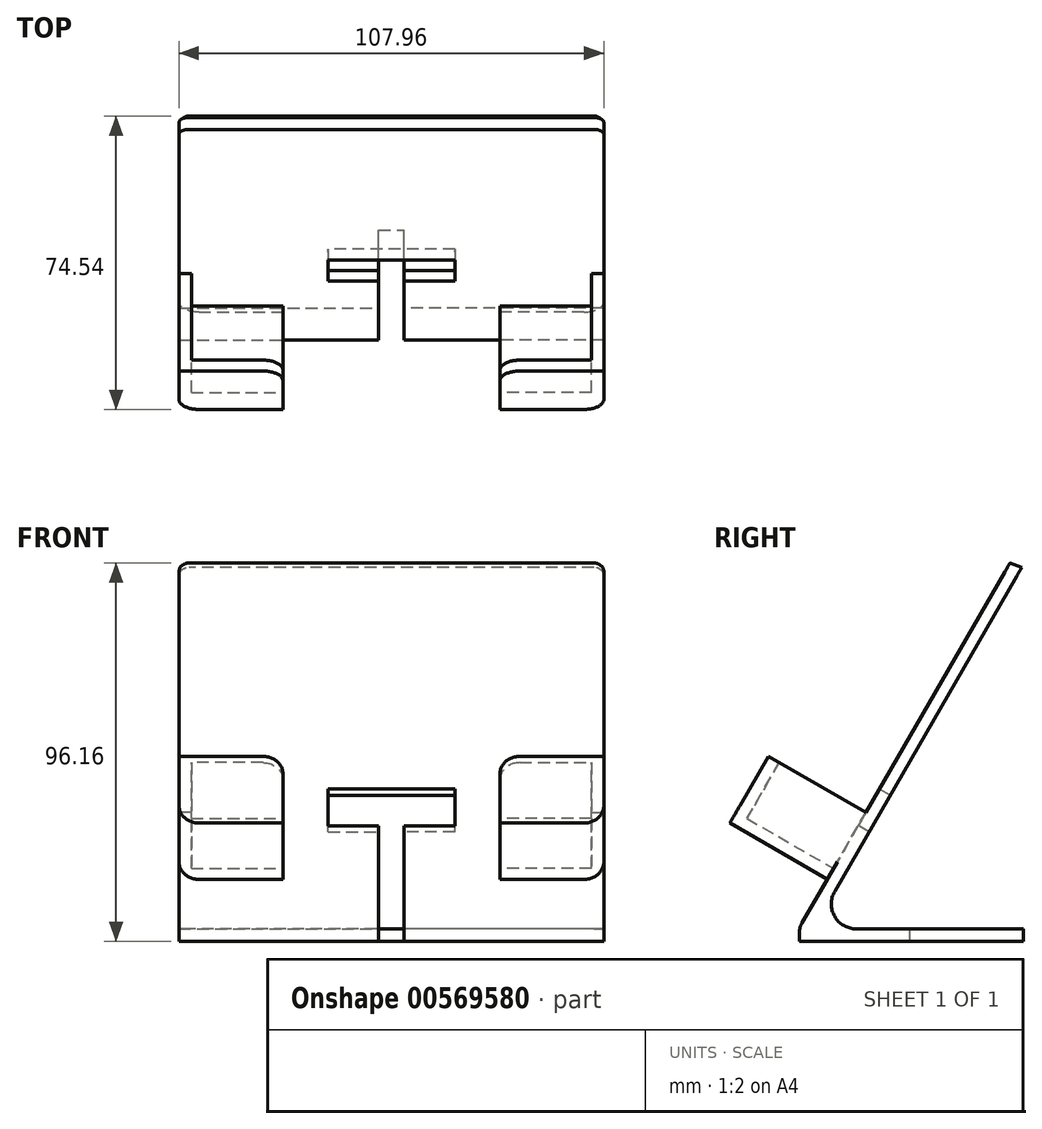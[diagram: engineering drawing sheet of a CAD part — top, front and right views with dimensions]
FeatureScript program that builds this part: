
annotation { "Feature Type Name" : "Feature", "Feature Type Description" : "" }
export const myFeature = defineFeature(function(context is Context, id is Id, definition is map)
    precondition{}
    {
        {
            var Q0;
            Q0=qCreatedBy(makeId("Right.planeOp"),FACE);
            var sketch = newSketch(context, id + "F0", { "sketchPlane" : qUnion([Q0])});
            skLineSegment(sketch, "E0", {"start": v(56.9, 0) * mm, "end": v(0, 0) * mm});
            skLineSegment(sketch, "E1", {"start": v(0, 0) * mm, "end": v(0, 3.5) * mm});
            skPoint(sketch, "E2.visualSharp", {"position": v(0, 0) * mm});
            skLineSegment(sketch, "E3", {"start": v(0, 3.5) * mm, "end": v(53.5, 96.16) * mm});
            skLineSegment(sketch, "E4.0", {"start": v(8.98, 12.7) * mm, "end": v(56.54, 95.07) * mm});
            skLineSegment(sketch, "E4.2", {"start": v(56.9, 3.18) * mm, "end": v(14.48, 3.17) * mm});
            skLineSegment(sketch, "E5", {"start": v(53.5, 96.16) * mm, "end": v(56.54, 95.07) * mm});
            skLineSegment(sketch, "E6", {"start": v(56.9, 3.18) * mm, "end": v(56.9, 0) * mm});
            skPoint(sketch, "E7.visualSharp", {"position": v(3.48, 3.17) * mm});
            skArc(sketch, "E7.filletArc", {"start": v(8.98, 12.7) * mm, "mid": v(8.98, 6.35) * mm, "end": v(14.48, 3.17) * mm});
            skSolve(sketch);
        }
        {
            var Q0;
            Q0=qSketchRegion(id+"F0",true);
            extrude(context, id + "F1", {"entities" : qUnion([Q0]), "depth" : 53.97 * mm, "offsetDistance" : 25.4 * mm});
        }
        {
            var Q0;
            {var subQ0=makeQuery(id+"F1.opExtrude","SWEPT_FACE",FACE,{"disambiguationData":[OSD([sQuery(id+"F0.wireOp",EDGE,"E3")])]});Q0=makeQuery(id+"F12.boolean.opBoolean","MERGE",FACE,{"derivedFrom":[subQ0,makeQuery(id+"F12.opPattern","COPY",FACE,{"derivedFrom":subQ0,"instanceName":"1"})]});}
            var sketch = newSketch(context, id + "F2", { "sketchPlane" : qUnion([Q0])});
            skLineSegment(sketch, "E8", {"start": v(53.98, 17.22) * mm, "end": v(27.55, 17.22) * mm});
            skLineSegment(sketch, "E9", {"start": v(53.98, 17.22) * mm, "end": v(53.98, 36.77) * mm});
            skLineSegment(sketch, "E10.0", {"start": v(50.8, 20.4) * mm, "end": v(50.8, 36.77) * mm});
            skLineSegment(sketch, "E10.1", {"start": v(50.8, 20.4) * mm, "end": v(27.55, 20.4) * mm});
            skLineSegment(sketch, "E11", {"start": v(50.8, 36.77) * mm, "end": v(53.98, 36.77) * mm});
            skLineSegment(sketch, "E12", {"start": v(27.55, 20.4) * mm, "end": v(27.55, 17.22) * mm});
            skSolve(sketch);
        }
        {
            var Q0;
            Q0=qSketchRegion(id+"F2",true);
            extrude(context, id + "F3", {"entities" : qUnion([Q0]), "operationType" : NewBodyOperationType.ADD, "depth" : 25.4 * mm, "offsetDistance" : 25.4 * mm});
        }
        {
            var Q0;
            {var subQ0=makeQuery(id+"F1.opExtrude","SWEPT_FACE",FACE,{"disambiguationData":[OSD([sQuery(id+"F0.wireOp",EDGE,"E3")])]});Q0=makeQuery(id+"F12.boolean.opBoolean","MERGE",FACE,{"derivedFrom":[subQ0,makeQuery(id+"F12.opPattern","COPY",FACE,{"derivedFrom":subQ0,"instanceName":"1"})]});}
            var sketch = newSketch(context, id + "F4", { "sketchPlane" : qUnion([Q0])});
            skLineSegment(sketch, "E13.bottom", {"start": v(0, 43.7) * mm, "end": v(16.1, 43.7) * mm});
            skLineSegment(sketch, "E13.top", {"start": v(0, 32.91) * mm, "end": v(16.1, 32.91) * mm});
            skLineSegment(sketch, "E13.left", {"start": v(0, 43.7) * mm, "end": v(0, 32.91) * mm});
            skLineSegment(sketch, "E13.right", {"start": v(16.1, 43.7) * mm, "end": v(16.1, 32.91) * mm});
            skSolve(sketch);
        }
        {
            var Q0;
            Q0=qSketchRegion(id+"F4",true);
            extrude(context, id + "F5", {"entities" : qUnion([Q0]), "operationType" : NewBodyOperationType.REMOVE, "endBound" : BoundingType.UP_TO_NEXT, "oppositeDirection" : true, "depth" : 25.4 * mm});
        }
        {
            var Q0;
            Q0=qCreatedBy(makeId("Top.planeOp"),FACE);
            var sketch = newSketch(context, id + "F6", { "sketchPlane" : qUnion([Q0])});
            skLineSegment(sketch, "E14.bottom", {"start": v(0, 0) * mm, "end": v(3.24, 0) * mm});
            skLineSegment(sketch, "E14.top", {"start": v(0, 27.97) * mm, "end": v(3.24, 27.97) * mm});
            skLineSegment(sketch, "E14.left", {"start": v(0, 0) * mm, "end": v(0, 27.97) * mm});
            skLineSegment(sketch, "E14.right", {"start": v(3.24, 0) * mm, "end": v(3.24, 27.97) * mm});
            skSolve(sketch);
        }
        {
            var Q0;
            Q0=qSketchRegion(id+"F6",true);
            var Q1;
            {var subQ0=makeQuery(id+"F5.boolean.opBoolean","COPY",FACE,{"derivedFrom":makeQuery(id+"F5.opExtrude","SWEPT_FACE",FACE,{"disambiguationData":[OSD([sQuery(id+"F4.wireOp",EDGE,"E13.top")])]})});Q1=makeQuery(id+"F12.boolean.opBoolean","MERGE",FACE,{"derivedFrom":[subQ0,makeQuery(id+"F12.opPattern","COPY",FACE,{"derivedFrom":subQ0,"instanceName":"1"})]});}
            extrude(context, id + "F7", {"entities" : qUnion([Q0]), "operationType" : NewBodyOperationType.REMOVE, "endBound" : BoundingType.UP_TO_SURFACE, "endBoundEntityFace" : qUnion([Q1]), "depth" : 25.4 * mm, "offsetDistance" : 25.4 * mm});
        }
        {
            var Q0;
            Q0=makeQuery(id+"F3.opExtrude","CAP_FACE",FACE,{"disambiguationData":[OSD([sQuery(id+"F2.wireOp",EDGE,"E8"),sQuery(id+"F2.wireOp",EDGE,"E9"),sQuery(id+"F2.wireOp",EDGE,"E10.0"),sQuery(id+"F2.wireOp",EDGE,"E10.1"),sQuery(id+"F2.wireOp",EDGE,"E11"),sQuery(id+"F2.wireOp",EDGE,"E12")])],"isStart":false});
            var sketch = newSketch(context, id + "F8", { "sketchPlane" : qUnion([Q0])});
            skLineSegment(sketch, "E15.bottom", {"start": v(53.98, 17.22) * mm, "end": v(27.55, 17.22) * mm});
            skLineSegment(sketch, "E15.top", {"start": v(53.97, 36.77) * mm, "end": v(27.55, 36.77) * mm});
            skLineSegment(sketch, "E15.left", {"start": v(53.97, 17.22) * mm, "end": v(53.97, 36.77) * mm});
            skLineSegment(sketch, "E15.right", {"start": v(27.55, 17.22) * mm, "end": v(27.55, 36.77) * mm});
            skSolve(sketch);
        }
        {
            var Q0;
            Q0=qSketchRegion(id+"F8",true);
            extrude(context, id + "F9", {"entities" : qUnion([Q0]), "operationType" : NewBodyOperationType.ADD, "depth" : 3.17 * mm, "offsetDistance" : 25.4 * mm});
        }
        {
            var Q0;
            Q0=makeQuery(id+"F1.opExtrude","SWEPT_EDGE",EDGE,{"disambiguationData":[OSD([sQuery(id+"F0.wireOp",EDGE,"E1"),sQuery(id+"F0.wireOp",EDGE,"E3")])]});
            var Q1;
            Q1=makeQuery(id+"F9.boolean.opBoolean","MERGE",EDGE,{"derivedFrom":[makeQuery(id+"F3.opExtrude","SWEPT_EDGE",EDGE,{"disambiguationData":[OSD([sQuery(id+"F0.wireOp",EDGE,"E3"),sQuery(id+"F2.wireOp",EDGE,"E8"),sQuery(id+"F2.wireOp",EDGE,"E9")])]}),makeQuery(id+"F9.opExtrude","SWEPT_EDGE",EDGE,{"disambiguationData":[OSD([sQuery(id+"F8.wireOp",EDGE,"E15.bottom"),sQuery(id+"F8.wireOp",EDGE,"E15.left")])]})]});
            var Q2;
            Q2=makeQuery(id+"F9.opExtrude","SWEPT_EDGE",EDGE,{"disambiguationData":[OSD([sQuery(id+"F8.wireOp",EDGE,"E15.top"),sQuery(id+"F8.wireOp",EDGE,"E15.right")])]});
            fillet(context, id + "F10", {"entities" : qUnion([Q0, Q1, Q2]), "radius" : 5.08 * mm, "tangentPropagation" : true, "allowEdgeOverflow" : false});
        }
        {
            var Q0;
            Q0=makeQuery(id+"F1.opExtrude","CAP_EDGE",EDGE,{"disambiguationData":[OSD([sQuery(id+"F0.wireOp",EDGE,"E5")])],"isStart":false});
            var Q1;
            Q1=makeQuery(id+"F1.opExtrude","CAP_EDGE",EDGE,{"disambiguationData":[OSD([sQuery(id+"F0.wireOp",EDGE,"E6")])],"isStart":false});
            var Q2;
            Q2=makeQuery(id+"F7.boolean.opBoolean","COPY",EDGE,{"derivedFrom":makeQuery(id+"F7.opExtrude","CAP_EDGE",EDGE,{"disambiguationData":[OSD([sQuery(id+"F6.wireOp",EDGE,"E14.right")])],"isStart":false})});
            fillet(context, id + "F11", {"entities" : qUnion([Q0, Q1, Q2]), "radius" : 2.54 * mm, "tangentPropagation" : true, "allowEdgeOverflow" : false});
        }
        {
            var Q0;
            Q0=makeQuery(id+"F1.opExtrude","SWEPT_BODY",BODY,{"disambiguationData":[OSD([sQuery(id+"F0.wireOp",EDGE,"E0"),sQuery(id+"F0.wireOp",EDGE,"E1"),sQuery(id+"F0.wireOp",EDGE,"E3"),sQuery(id+"F0.wireOp",EDGE,"E4.0"),sQuery(id+"F0.wireOp",EDGE,"E4.1"),sQuery(id+"F0.wireOp",EDGE,"E4.2"),sQuery(id+"F0.wireOp",EDGE,"E5"),sQuery(id+"F0.wireOp",EDGE,"E6")])]});
            var Q1;
            Q1=qCreatedBy(makeId("Right.planeOp"),FACE);
            mirror(context, id + "F12", {"operationType" : NewBodyOperationType.ADD, "entities" : qUnion([Q0]), "mirrorPlane" : qUnion([Q1])});
        }
    });
